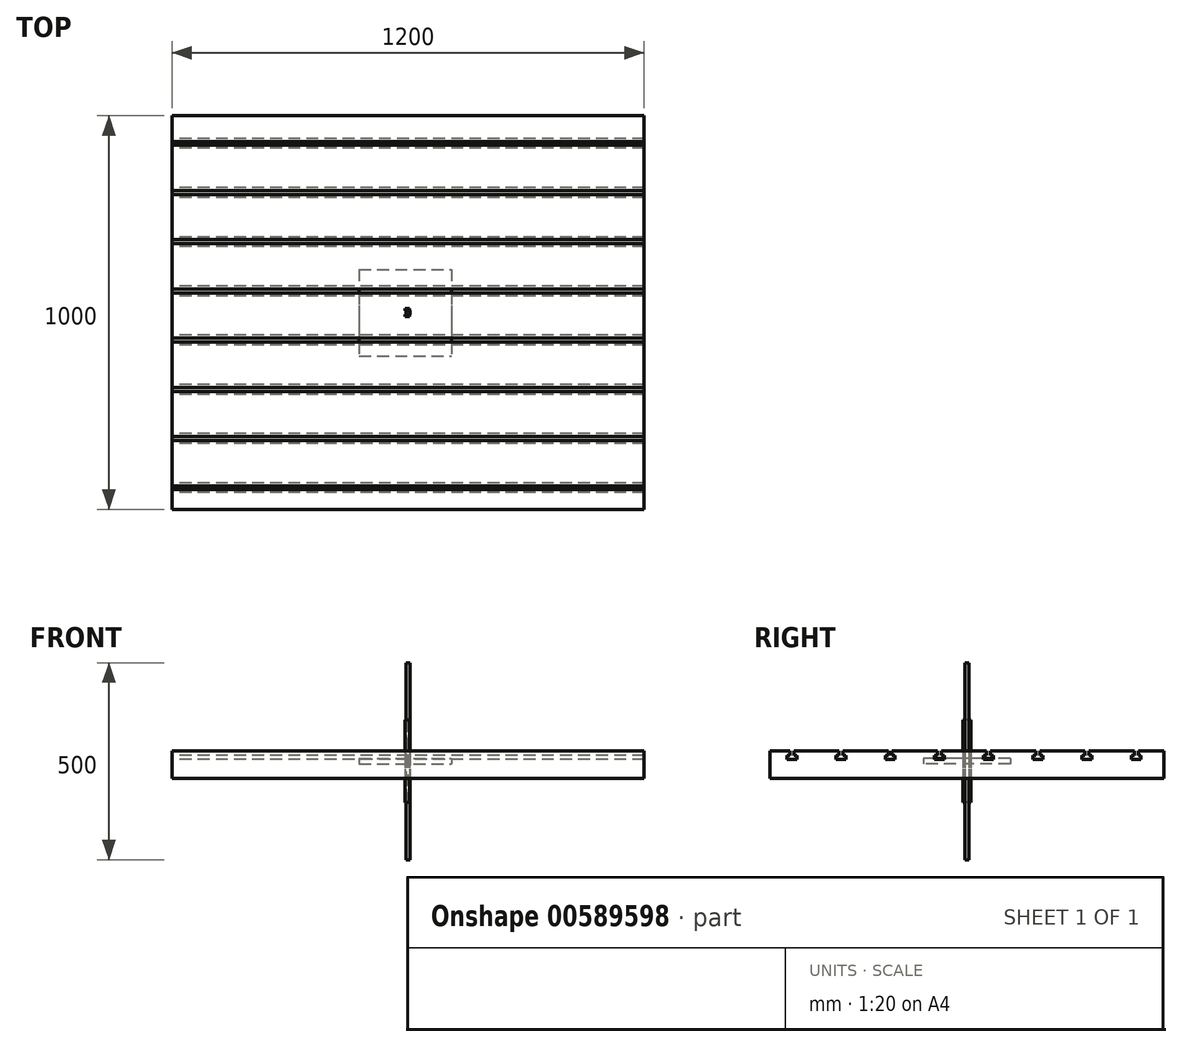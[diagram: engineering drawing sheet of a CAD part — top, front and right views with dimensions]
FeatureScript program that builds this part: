
annotation { "Feature Type Name" : "Feature", "Feature Type Description" : "" }
export const myFeature = defineFeature(function(context is Context, id is Id, definition is map)
    precondition{}
    {
        {
            var Q0;
            Q0=qCreatedBy(makeId("Right.planeOp"),FACE);
            var sketch = newSketch(context, id + "F0", { "sketchPlane" : qUnion([Q0])});
            skLineSegment(sketch, "E0.bottom", {"start": v(-500, 27.01) * mm, "end": v(-450, 27.01) * mm});
            skLineSegment(sketch, "E0.top", {"start": v(-500, -42.99) * mm, "end": v(500, -42.99) * mm});
            skLineSegment(sketch, "E0.left", {"start": v(-500, 27.01) * mm, "end": v(-500, -42.99) * mm});
            skLineSegment(sketch, "E0.right", {"start": v(500, 27.01) * mm, "end": v(500, -42.99) * mm});
            skLineSegment(sketch, "E1.bottom", {"start": v(-457.5, 5.01) * mm, "end": v(-432.5, 5.01) * mm});
            skLineSegment(sketch, "E1.top", {"start": v(-457.5, 15.01) * mm, "end": v(-450, 15.01) * mm});
            skLineSegment(sketch, "E1.left", {"start": v(-457.5, 5.01) * mm, "end": v(-457.5, 15.01) * mm});
            skLineSegment(sketch, "E1.right", {"start": v(-432.5, 5.01) * mm, "end": v(-432.5, 15.01) * mm});
            skLineSegment(sketch, "E2", {"start": v(-450, 15.01) * mm, "end": v(-450, 27.01) * mm});
            skLineSegment(sketch, "E3", {"start": v(-440, 15.01) * mm, "end": v(-440, 27.01) * mm});
            skLineSegment(sketch, "E4.trimOffspring", {"start": v(-440, 27.01) * mm, "end": v(-325, 27.01) * mm});
            skLineSegment(sketch, "E5.trimOffspring", {"start": v(-440, 15.01) * mm, "end": v(-432.5, 15.01) * mm});
            skLineSegment(sketch, "E6.1.0.0", {"start": v(-332.5, 15.01) * mm, "end": v(-325, 15.01) * mm});
            skLineSegment(sketch, "E6.1.0.1", {"start": v(-325, 15.01) * mm, "end": v(-325, 27.01) * mm});
            skLineSegment(sketch, "E6.1.0.2", {"start": v(-307.5, 5.01) * mm, "end": v(-307.5, 15.01) * mm});
            skLineSegment(sketch, "E6.1.0.3", {"start": v(-332.5, 5.01) * mm, "end": v(-307.5, 5.01) * mm});
            skLineSegment(sketch, "E6.1.0.4", {"start": v(-332.5, 5.01) * mm, "end": v(-332.5, 15.01) * mm});
            skLineSegment(sketch, "E6.1.0.5", {"start": v(-315, 15.01) * mm, "end": v(-315, 27.01) * mm});
            skLineSegment(sketch, "E6.1.0.6", {"start": v(-315, 27.01) * mm, "end": v(-200, 27.01) * mm});
            skLineSegment(sketch, "E6.1.0.7", {"start": v(-315, 15.01) * mm, "end": v(-307.5, 15.01) * mm});
            skLineSegment(sketch, "E6.1.0.8", {"start": v(-375, 27.01) * mm, "end": v(-325, 27.01) * mm});
            skLineSegment(sketch, "E6.2.0.0", {"start": v(-207.5, 15.01) * mm, "end": v(-200, 15.01) * mm});
            skLineSegment(sketch, "E6.2.0.1", {"start": v(-200, 15.01) * mm, "end": v(-200, 27.01) * mm});
            skLineSegment(sketch, "E6.2.0.2", {"start": v(-182.5, 5.01) * mm, "end": v(-182.5, 15.01) * mm});
            skLineSegment(sketch, "E6.2.0.3", {"start": v(-207.5, 5.01) * mm, "end": v(-182.5, 5.01) * mm});
            skLineSegment(sketch, "E6.2.0.4", {"start": v(-207.5, 5.01) * mm, "end": v(-207.5, 15.01) * mm});
            skLineSegment(sketch, "E6.2.0.5", {"start": v(-190, 15.01) * mm, "end": v(-190, 27.01) * mm});
            skLineSegment(sketch, "E6.2.0.6", {"start": v(-190, 27.01) * mm, "end": v(-75, 27.01) * mm});
            skLineSegment(sketch, "E6.2.0.7", {"start": v(-190, 15.01) * mm, "end": v(-182.5, 15.01) * mm});
            skLineSegment(sketch, "E6.2.0.8", {"start": v(-250, 27.01) * mm, "end": v(-200, 27.01) * mm});
            skLineSegment(sketch, "E6.3.0.0", {"start": v(-82.5, 15.01) * mm, "end": v(-75, 15.01) * mm});
            skLineSegment(sketch, "E6.3.0.1", {"start": v(-75, 15.01) * mm, "end": v(-75, 27.01) * mm});
            skLineSegment(sketch, "E6.3.0.2", {"start": v(-57.5, 5.01) * mm, "end": v(-57.5, 15.01) * mm});
            skLineSegment(sketch, "E6.3.0.3", {"start": v(-82.5, 5.01) * mm, "end": v(-57.5, 5.01) * mm});
            skLineSegment(sketch, "E6.3.0.4", {"start": v(-82.5, 5.01) * mm, "end": v(-82.5, 15.01) * mm});
            skLineSegment(sketch, "E6.3.0.5", {"start": v(-65, 15.01) * mm, "end": v(-65, 27.01) * mm});
            skLineSegment(sketch, "E6.3.0.6", {"start": v(-65, 27.01) * mm, "end": v(50, 27.01) * mm});
            skLineSegment(sketch, "E6.3.0.7", {"start": v(-65, 15.01) * mm, "end": v(-57.5, 15.01) * mm});
            skLineSegment(sketch, "E6.3.0.8", {"start": v(-125, 27.01) * mm, "end": v(-75, 27.01) * mm});
            skLineSegment(sketch, "E6.4.0.0", {"start": v(42.5, 15.01) * mm, "end": v(50, 15.01) * mm});
            skLineSegment(sketch, "E6.4.0.1", {"start": v(50, 15.01) * mm, "end": v(50, 27.01) * mm});
            skLineSegment(sketch, "E6.4.0.2", {"start": v(67.5, 5.01) * mm, "end": v(67.5, 15.01) * mm});
            skLineSegment(sketch, "E6.4.0.3", {"start": v(42.5, 5.01) * mm, "end": v(67.5, 5.01) * mm});
            skLineSegment(sketch, "E6.4.0.4", {"start": v(42.5, 5.01) * mm, "end": v(42.5, 15.01) * mm});
            skLineSegment(sketch, "E6.4.0.5", {"start": v(60, 15.01) * mm, "end": v(60, 27.01) * mm});
            skLineSegment(sketch, "E6.4.0.6", {"start": v(60, 27.01) * mm, "end": v(175, 27.01) * mm});
            skLineSegment(sketch, "E6.4.0.7", {"start": v(60, 15.01) * mm, "end": v(67.5, 15.01) * mm});
            skLineSegment(sketch, "E6.4.0.8", {"start": v(0, 27.01) * mm, "end": v(50, 27.01) * mm});
            skLineSegment(sketch, "E6.5.0.0", {"start": v(167.5, 15.01) * mm, "end": v(175, 15.01) * mm});
            skLineSegment(sketch, "E6.5.0.1", {"start": v(175, 15.01) * mm, "end": v(175, 27.01) * mm});
            skLineSegment(sketch, "E6.5.0.2", {"start": v(192.5, 5.01) * mm, "end": v(192.5, 15.01) * mm});
            skLineSegment(sketch, "E6.5.0.3", {"start": v(167.5, 5.01) * mm, "end": v(192.5, 5.01) * mm});
            skLineSegment(sketch, "E6.5.0.4", {"start": v(167.5, 5.01) * mm, "end": v(167.5, 15.01) * mm});
            skLineSegment(sketch, "E6.5.0.5", {"start": v(185, 15.01) * mm, "end": v(185, 27.01) * mm});
            skLineSegment(sketch, "E6.5.0.6", {"start": v(185, 27.01) * mm, "end": v(300, 27.01) * mm});
            skLineSegment(sketch, "E6.5.0.7", {"start": v(185, 15.01) * mm, "end": v(192.5, 15.01) * mm});
            skLineSegment(sketch, "E6.5.0.8", {"start": v(125, 27.01) * mm, "end": v(175, 27.01) * mm});
            skLineSegment(sketch, "E6.6.0.0", {"start": v(292.5, 15.01) * mm, "end": v(300, 15.01) * mm});
            skLineSegment(sketch, "E6.6.0.1", {"start": v(300, 15.01) * mm, "end": v(300, 27.01) * mm});
            skLineSegment(sketch, "E6.6.0.2", {"start": v(317.5, 5.01) * mm, "end": v(317.5, 15.01) * mm});
            skLineSegment(sketch, "E6.6.0.3", {"start": v(292.5, 5.01) * mm, "end": v(317.5, 5.01) * mm});
            skLineSegment(sketch, "E6.6.0.4", {"start": v(292.5, 5.01) * mm, "end": v(292.5, 15.01) * mm});
            skLineSegment(sketch, "E6.6.0.5", {"start": v(310, 15.01) * mm, "end": v(310, 27.01) * mm});
            skLineSegment(sketch, "E6.6.0.6", {"start": v(310, 27.01) * mm, "end": v(425, 27.01) * mm});
            skLineSegment(sketch, "E6.6.0.7", {"start": v(310, 15.01) * mm, "end": v(317.5, 15.01) * mm});
            skLineSegment(sketch, "E6.6.0.8", {"start": v(250, 27.01) * mm, "end": v(300, 27.01) * mm});
            skLineSegment(sketch, "E6.7.0.0", {"start": v(417.5, 15.01) * mm, "end": v(425, 15.01) * mm});
            skLineSegment(sketch, "E6.7.0.1", {"start": v(425, 15.01) * mm, "end": v(425, 27.01) * mm});
            skLineSegment(sketch, "E6.7.0.2", {"start": v(442.5, 5.01) * mm, "end": v(442.5, 15.01) * mm});
            skLineSegment(sketch, "E6.7.0.3", {"start": v(417.5, 5.01) * mm, "end": v(442.5, 5.01) * mm});
            skLineSegment(sketch, "E6.7.0.4", {"start": v(417.5, 5.01) * mm, "end": v(417.5, 15.01) * mm});
            skLineSegment(sketch, "E6.7.0.5", {"start": v(435, 15.01) * mm, "end": v(435, 27.01) * mm});
            skLineSegment(sketch, "E6.7.0.6", {"start": v(435, 27.01) * mm, "end": v(500, 27.01) * mm});
            skLineSegment(sketch, "E6.7.0.7", {"start": v(435, 15.01) * mm, "end": v(442.5, 15.01) * mm});
            skLineSegment(sketch, "E6.7.0.8", {"start": v(375, 27.01) * mm, "end": v(425, 27.01) * mm});
            skLineSegment(sketch, "E6.direction1", {"start": v(-500, 27.01) * mm, "end": v(-375, 27.01) * mm, "construction": true});
            skLineSegment(sketch, "E7.trimOffspring", {"start": v(-190, 27.01) * mm, "end": v(-125, 27.01) * mm});
            skLineSegment(sketch, "E8.trimOffspring", {"start": v(310, 27.01) * mm, "end": v(375, 27.01) * mm});
            skLineSegment(sketch, "E9.trimOffspring", {"start": v(185, 27.01) * mm, "end": v(250, 27.01) * mm});
            skLineSegment(sketch, "E10.trimOffspring", {"start": v(60, 27.01) * mm, "end": v(125, 27.01) * mm});
            skSolve(sketch);
        }
        {
            var Q0;
            Q0=makeQuery(id+"F0.imprint","IMPRINT",FACE,{"disambiguationData":[TD([[makeQuery(id+"F0.imprint","IMPRINT",EDGE,{"derivedFrom":sQuery(id+"F0.wireOp",EDGE,"E0.bottom")}),-1.0]])]});
            extrude(context, id + "F1", {"entities" : qUnion([Q0]), "depth" : 600 * mm, "offsetDistance" : 25 * mm, "hasSecondDirection" : true, "secondDirectionOppositeDirection" : true, "secondDirectionDepth" : 600 * mm});
        }
        {
            var Q0;
            Q0=qCreatedBy(makeId("Top.planeOp"),FACE);
            var sketch = newSketch(context, id + "F2", { "sketchPlane" : qUnion([Q0])});
            skLineSegment(sketch, "E11.bottom", {"start": v(-140, 95) * mm, "end": v(90, 95) * mm});
            skLineSegment(sketch, "E11.top", {"start": v(-140, -95) * mm, "end": v(90, -95) * mm});
            skLineSegment(sketch, "E11.left", {"start": v(-140, 95) * mm, "end": v(-140, -95) * mm});
            skLineSegment(sketch, "E11.right", {"start": v(140, 55) * mm, "end": v(140, -45) * mm});
            skCircle(sketch, "E12", {"center": v(-110, 60) * mm, "radius": 12.5 * mm});
            skCircle(sketch, "E13.0.1.0", {"center": v(-110, 0) * mm, "radius": 12.5 * mm});
            skCircle(sketch, "E13.0.2.0", {"center": v(-110, -60) * mm, "radius": 12.5 * mm});
            skCircle(sketch, "E13.1.0.0", {"center": v(-40, 60) * mm, "radius": 12.5 * mm});
            skCircle(sketch, "E13.1.1.0", {"center": v(-40, 0) * mm, "radius": 12.5 * mm});
            skCircle(sketch, "E13.1.2.0", {"center": v(-40, -60) * mm, "radius": 12.5 * mm});
            skCircle(sketch, "E13.2.0.0", {"center": v(30, 60) * mm, "radius": 12.5 * mm});
            skCircle(sketch, "E13.2.1.0", {"center": v(30, 0) * mm, "radius": 12.5 * mm});
            skCircle(sketch, "E13.2.2.0", {"center": v(30, -60) * mm, "radius": 12.5 * mm});
            skLineSegment(sketch, "E13.direction1", {"start": v(-110, 60) * mm, "end": v(-40, 60) * mm, "construction": true});
            skLineSegment(sketch, "E13.direction2", {"start": v(-110, 60) * mm, "end": v(-110, 0) * mm, "construction": true});
            skLineSegment(sketch, "E14", {"start": v(90, 95) * mm, "end": v(140, 55) * mm});
            skLineSegment(sketch, "E15", {"start": v(90, -95) * mm, "end": v(140, -45) * mm});
            skCircle(sketch, "E16", {"center": v(130, 0) * mm, "radius": 5 * mm});
            skPoint(sketch, "E17.orphan", {"position": v(140, 95) * mm});
            skPoint(sketch, "E18.orphan", {"position": v(140, -95) * mm});
            skSolve(sketch);
        }
        {
            var Q0;
            Q0=makeQuery(id+"F2.imprint","IMPRINT",FACE,{"disambiguationData":[TD([[makeQuery(id+"F2.imprint","IMPRINT",EDGE,{"derivedFrom":sQuery(id+"F2.wireOp",EDGE,"E11.bottom")}),-1.0]])]});
            extrude(context, id + "F3", {"entities" : qUnion([Q0]), "depth" : 4 * mm, "offsetDistance" : 25 * mm, "hasSecondDirection" : true, "secondDirectionOppositeDirection" : true, "secondDirectionDepth" : 4 * mm});
        }
        {
            var Q0;
            Q0=makeQuery(id+"F3.opExtrude","CAP_FACE",FACE,{"disambiguationData":[OSD([sQuery(id+"F2.wireOp",EDGE,"E11.bottom"),sQuery(id+"F2.wireOp",EDGE,"E11.top"),sQuery(id+"F2.wireOp",EDGE,"E11.left"),sQuery(id+"F2.wireOp",EDGE,"E11.right"),sQuery(id+"F2.wireOp",EDGE,"E12"),sQuery(id+"F2.wireOp",EDGE,"E13.0.1.0"),sQuery(id+"F2.wireOp",EDGE,"E13.0.2.0"),sQuery(id+"F2.wireOp",EDGE,"E13.1.0.0"),sQuery(id+"F2.wireOp",EDGE,"E13.1.1.0"),sQuery(id+"F2.wireOp",EDGE,"E13.1.2.0"),sQuery(id+"F2.wireOp",EDGE,"E13.2.0.0"),sQuery(id+"F2.wireOp",EDGE,"E13.2.1.0"),sQuery(id+"F2.wireOp",EDGE,"E13.2.2.0"),sQuery(id+"F2.wireOp",EDGE,"E14"),sQuery(id+"F2.wireOp",EDGE,"E15"),sQuery(id+"F2.wireOp",EDGE,"E16")])],"isStart":false});
            var sketch = newSketch(context, id + "F4", { "sketchPlane" : qUnion([Q0])});
            skCircle(sketch, "E19", {"center": v(130, 0) * mm, "radius": 5 * mm});
            skSolve(sketch);
        }
        {
            var Q0;
            Q0=makeQuery(id+"F4.imprint","IMPRINT",FACE,{"disambiguationData":[TD([[makeQuery(id+"F4.imprint","IMPRINT",EDGE,{"derivedFrom":sQuery(id+"F4.wireOp",EDGE,"E19")}),1.0]])]});
            extrude(context, id + "F5", {"entities" : qUnion([Q0]), "operationType" : NewBodyOperationType.ADD, "depth" : 15 * mm, "offsetDistance" : 25 * mm, "hasSecondDirection" : true, "secondDirectionOppositeDirection" : true, "secondDirectionDepth" : 23 * mm});
        }
        {
            var Q0;
            Q0=qCreatedBy(makeId("Top.planeOp"),FACE);
            var sketch = newSketch(context, id + "F6", { "sketchPlane" : qUnion([Q0])});
            skLineSegment(sketch, "E20.bottom", {"start": v(-5, 5) * mm, "end": v(5, 5) * mm});
            skLineSegment(sketch, "E20.top", {"start": v(-5, -5) * mm, "end": v(5, -5) * mm});
            skLineSegment(sketch, "E20.left", {"start": v(-5, 5) * mm, "end": v(-5, -5) * mm});
            skLineSegment(sketch, "E20.right", {"start": v(5, 5) * mm, "end": v(5, -5) * mm});
            skSolve(sketch);
        }
        {
            var Q0;
            Q0=makeQuery(id+"F6.imprint","IMPRINT",FACE,{"disambiguationData":[TD([[makeQuery(id+"F6.imprint","IMPRINT",EDGE,{"derivedFrom":sQuery(id+"F6.wireOp",EDGE,"E20.bottom")}),-1.0]])]});
            extrude(context, id + "F7", {"entities" : qUnion([Q0]), "depth" : 250 * mm, "offsetDistance" : 25 * mm, "hasSecondDirection" : true, "secondDirectionOppositeDirection" : true, "secondDirectionDepth" : 250 * mm});
        }
        {
            var Q0;
            Q0=qCreatedBy(makeId("Top.planeOp"),FACE);
            var sketch = newSketch(context, id + "F8", { "sketchPlane" : qUnion([Q0])});
            skLineSegment(sketch, "E21.bottom", {"start": v(-7.5, 10) * mm, "end": v(4.5, 10) * mm});
            skLineSegment(sketch, "E21.top", {"start": v(-7.5, -10) * mm, "end": v(4.5, -10) * mm});
            skLineSegment(sketch, "E21.left", {"start": v(-7.5, 10) * mm, "end": v(-7.5, 5) * mm});
            skLineSegment(sketch, "E21.right", {"start": v(4.5, 10) * mm, "end": v(4.5, -10) * mm});
            skLineSegment(sketch, "E22", {"start": v(-7.5, 5) * mm, "end": v(0, 5) * mm});
            skLineSegment(sketch, "E23", {"start": v(0, 5) * mm, "end": v(0, -5) * mm});
            skLineSegment(sketch, "E24", {"start": v(0, -5) * mm, "end": v(-7.5, -5) * mm});
            skLineSegment(sketch, "E25.trimOffspring", {"start": v(-7.5, -5) * mm, "end": v(-7.5, -10) * mm});
            skSolve(sketch);
        }
        {
            var Q0;
            Q0=makeQuery(id+"F8.imprint","IMPRINT",FACE,{"disambiguationData":[TD([[makeQuery(id+"F8.imprint","IMPRINT",EDGE,{"derivedFrom":sQuery(id+"F8.wireOp",EDGE,"E21.bottom")}),-1.0]])]});
            extrude(context, id + "F9", {"entities" : qUnion([Q0]), "depth" : 105 * mm, "offsetDistance" : 25 * mm, "hasSecondDirection" : true, "secondDirectionOppositeDirection" : true, "secondDirectionDepth" : 105 * mm});
        }
        {
            var Q0;
            Q0=qCreatedBy(makeId("Top.planeOp"),FACE);
            var sketch = newSketch(context, id + "F10", { "sketchPlane" : qUnion([Q0])});
            skLineSegment(sketch, "E26.bottom", {"start": v(-124, 110) * mm, "end": v(110, 110) * mm});
            skLineSegment(sketch, "E26.top", {"start": v(-124, -110) * mm, "end": v(110, -110) * mm});
            skLineSegment(sketch, "E26.left", {"start": v(-124, 110) * mm, "end": v(-124, -110) * mm});
            skLineSegment(sketch, "E26.right", {"start": v(110, 110) * mm, "end": v(110, -110) * mm});
            skSolve(sketch);
        }
        {
            var Q0;
            Q0=makeQuery(id+"F10.imprint","IMPRINT",FACE,{"disambiguationData":[TD([[makeQuery(id+"F10.imprint","IMPRINT",EDGE,{"derivedFrom":sQuery(id+"F10.wireOp",EDGE,"E26.bottom")}),-1.0]])]});
            extrude(context, id + "F11", {"entities" : qUnion([Q0]), "depth" : 7 * mm, "offsetDistance" : 25 * mm, "hasSecondDirection" : true, "secondDirectionOppositeDirection" : true, "secondDirectionDepth" : 7 * mm});
        }
    });
